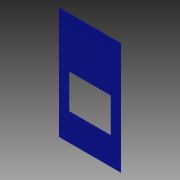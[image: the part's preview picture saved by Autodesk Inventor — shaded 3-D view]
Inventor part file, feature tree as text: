
AUTODESK INVENTOR PART (.ipt)
format: ipt  version: 2013 (Build 170138000, 138)  size: 80,896 bytes
history: native  units: in
note: dims shown in document units (in); Inventor stores cm internally (conversion verified against a paired STEP export)
features: extrude x2, sketch x2
ambient origin geometry x8: Origin, YZ Plane, XZ Plane, XY Plane, X Axis, Y Axis, Z Axis, Center Point
bodies: Solid1 (feature_tree)
feature tree (4):
  extrude  "Extrusion1"  Depth=78.0in
  extrude  "Extrusion2"  Depth=29.0in
  sketch  "Sketch1"  dims[d0=43.0in d1=78.0in]
  sketch  "Sketch2"  dims[d2=0.125in d3=0.0in d4=29.0in d6=24.0in d7=35.0in d8=7.0in d9=0.125in d10=0.0in]
